# Revit family: Camera-Security-iPRO-5MP_Vandal_Resistant_Indoor_Dome-Network-WV-S22500-V3LX
name_source: partatom
category: Security Devices
units: mm (PartAtom-declared; Revit-internal decimal feet)

## family parameters
Cut with Voids When Loaded = No
Host = Face
Maintain Annotation Orientation = No
OmniClass Number = 23.85.10.14.11
OmniClass Title = Cameras
Part Type = Normal
Room Calculation Point = No
Round Connector Dimension = Use Diameter
Shared = No

## types (1)
- WV-S22500-V3L
    Alarm Input Or Output Specification = ALARM IN 1 (Alarm input 1/ Black & white input/ Auto time adjustment input) (x1) ALARM IN 2 (Alarm input 2/ ALARM OUT) (x1) ALARM IN 3 (Alarm input 3/ AUX OUT) (x1)
    Angle Of View = 105
    Audio In = Yes
    Audio Out = Yes
    Communication Ports = 10Base-T / 100Base-TX, RJ45 connector
    Date Last Modified = 2022/08/04
    Day Or Night = Yes
    Default Elevation = 0 "
    Description = Security Camera, 5MP Vandal Resistant Indoor Dome Network Camera, WV-S22500-V3L
    Diameter = 5.1 "
    Equipment Abbreviation = SC
    Family Version = 1.0.0
    HFOV Max 169 = 105.00°
    HFOV Max 43 = 105.00°
    HFOV Min 169 = 33.00°
    HFOV Min 43 = 33.00°
    Has POE = Yes
    Height = 4.04 "
    IP Or Analog = IP
    Indoor Or Outdoor = Indoor
    Manufacturer = i-PRO Co., Ltd.
    Minimum Illumination = 0.050 lx
    Model = WV-S22500-V3L
    Model Disclaimer = Contact i-Pro for more information
    Mounting Positions = Mount Dependent or Surface Mount
    Operational Humidity = 10 to 90 % (no condensation)
    Operational Temperature = -10 °C to +50 °C (14 °F to 122 °F)
    Pan Max = 120.00°
    Pan Min = -240.00°
    Panning Range = -240 to +120
    Part Description = Security Camera, 5MP Vandal Resistant Indoor Dome Network Camera, WV-S22500-V3L
    Part Number = WV-S22500-V3L
    Product Documentation Link = https://bizpartner.panasonic.net
    Product Material = Paint - i-PRO White
    Product Page URL = https://i-pro.com
    Provide Feedback = https://i-pro.com
    Regulatory Compliance = UL (UL62368-1), c-UL (CSA C22.2 No.62368-1), CE, IEC62368-1, FCC (Part15 ClassA), ICES-003 ClassA, EN55032 ClassA, EN55035
    Storage Temperature = -10 °C to +50 °C (14 °F to 122 °F)
    Tilt Max = 85.00°
    Tilt Min = -30.00°
    Tilting Range = -30 to +85
    URL = https://i-pro.com
    VFOV Max 169 = 56.00°
    VFOV Max 43 = 76.00°
    VFOV Min 169 = 19.00°
    VFOV Min 43 = 25.00°
    Vandal Resistant = Yes
    Weight = 1.77 lb
    Wide Dynamic Range = Yes
    Yaw Max = 100.00°
    Yaw Min = -100.00°
    Yawing Range = -100 to +100
    z Base Height = 2.2 "
    z Base Radius = 2.55 "
    z Bracket Radius = 3.66 "
    z Const Pan Handle Length = 19.49 "
    z Const Tilt Base Length = 9.84 "
    z Const Tilt Base2 Length = 19.69 "
    z Const Tilt Handle Length = 11.81 "
    z Const Yaw Base Length = 10.24 "
    z Const Yaw Base2 Length = 17.32 "
    z Const Yaw Handle Length = 9.25 "
    z Dome Material = Glass - Smoked
    z Dome Radius = 1.83 "
    z VV Viewpoint Depth Max = 1.19 "
    z VV Viewpoint Depth Min = 1.19 "
    z Zero = 0 "

## geometry (parser evidence)
native form markers: Sweep x5
no freeform markers — native parametric forms only
